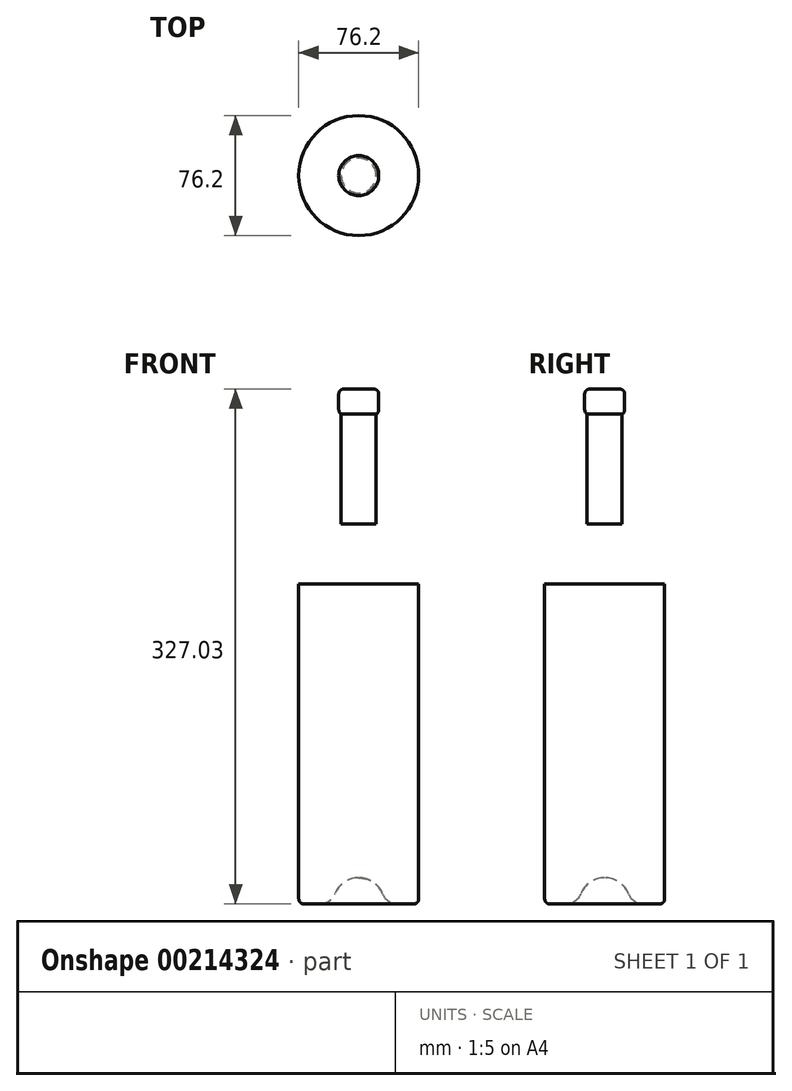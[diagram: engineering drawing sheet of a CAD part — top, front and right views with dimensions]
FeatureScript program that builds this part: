
annotation { "Feature Type Name" : "Feature", "Feature Type Description" : "" }
export const myFeature = defineFeature(function(context is Context, id is Id, definition is map)
    precondition{}
    {
        {
            var Q0;
            Q0=qCreatedBy(makeId("Front.planeOp"),FACE);
            var sketch = newSketch(context, id + "F0", { "sketchPlane" : qUnion([Q0])});
            skLineSegment(sketch, "E0.bottom", {"start": v(38.1, 101.6) * mm, "end": v(-38.1, 101.6) * mm});
            skLineSegment(sketch, "E0.top", {"start": v(38.1, -101.6) * mm, "end": v(24.45, -101.6) * mm});
            skLineSegment(sketch, "E0.left", {"start": v(38.1, 101.6) * mm, "end": v(38.1, -101.6) * mm});
            skLineSegment(sketch, "E0.right", {"start": v(-38.1, 101.6) * mm, "end": v(-38.1, -101.6) * mm});
            skPoint(sketch, "E0.middle", {"position": v(0, 0) * mm});
            skLineSegment(sketch, "E1.bottom", {"start": v(11.11, 225.42) * mm, "end": v(-11.11, 225.42) * mm});
            skLineSegment(sketch, "E1.top", {"start": v(11.11, 139.7) * mm, "end": v(-11.11, 139.7) * mm});
            skLineSegment(sketch, "E1.left", {"start": v(11.11, 225.42) * mm, "end": v(11.11, 139.7) * mm});
            skLineSegment(sketch, "E1.right", {"start": v(-11.11, 225.42) * mm, "end": v(-11.11, 139.7) * mm});
            skPoint(sketch, "E1.middle", {"position": v(0, 182.56) * mm});
            skLineSegment(sketch, "E2", {"start": v(0, 0) * mm, "end": v(0, 182.56) * mm, "construction": true});
            skLineSegment(sketch, "E3.bottom", {"start": v(12.7, 225.42) * mm, "end": v(-12.7, 225.42) * mm});
            skLineSegment(sketch, "E3.top", {"start": v(12.7, 209.55) * mm, "end": v(-12.7, 209.55) * mm});
            skLineSegment(sketch, "E3.left", {"start": v(12.7, 225.42) * mm, "end": v(12.7, 209.55) * mm});
            skLineSegment(sketch, "E3.right", {"start": v(-12.7, 225.42) * mm, "end": v(-12.7, 209.55) * mm});
            skPoint(sketch, "E3.middle", {"position": v(0, 217.49) * mm});
            skPoint(sketch, "E3.cornerSnap0", {"position": v(0, 225.42) * mm});
            skLineSegment(sketch, "E4", {"start": v(0, -85.04) * mm, "end": v(0, -101.6) * mm, "construction": true});
            skLineSegment(sketch, "E5.trimOffspring", {"start": v(-24.45, -101.6) * mm, "end": v(-38.1, -101.6) * mm});
            skArc(sketch, "E6", {"start": v(-24.45, -101.6) * mm, "mid": v(-18.89, -99.9) * mm, "end": v(-15.24, -95.36) * mm});
            skArc(sketch, "E7", {"start": v(-15.24, -95.36) * mm, "mid": v(-9.2, -87.87) * mm, "end": v(0, -85.04) * mm});
            skLineSegment(sketch, "E8", {"start": v(0, -85.04) * mm, "end": v(-15.84, -85.04) * mm, "construction": true});
            skArc(sketch, "E9.MirrorCS", {"start": v(15.24, -95.36) * mm, "mid": v(9.2, -87.87) * mm, "end": v(0, -85.04) * mm});
            skArc(sketch, "E10.MirrorCS", {"start": v(24.45, -101.6) * mm, "mid": v(18.89, -99.9) * mm, "end": v(15.24, -95.36) * mm});
            skArc(sketch, "E11", {"start": v(-38.1, 101.6) * mm, "mid": v(-34.06, 114.39) * mm, "end": v(-23.4, 122.53) * mm});
            skArc(sketch, "E12", {"start": v(-23.4, 122.53) * mm, "mid": v(-14.59, 129.2) * mm, "end": v(-11.11, 139.7) * mm});
            skArc(sketch, "E13.MirrorCS", {"start": v(23.4, 122.53) * mm, "mid": v(14.59, 129.2) * mm, "end": v(11.11, 139.7) * mm});
            skArc(sketch, "E14.MirrorCS", {"start": v(38.1, 101.6) * mm, "mid": v(34.06, 114.39) * mm, "end": v(23.4, 122.53) * mm});
            skLineSegment(sketch, "E15", {"start": v(0, -85.04) * mm, "end": v(0, 225.42) * mm});
            skSolve(sketch);
        }
        {
            var Q0;
            {var subQ5=sQuery(id+"F0.wireOp",EDGE,"E3.right");Q0=makeQuery(id+"F0.imprint","IMPRINT",FACE,{"disambiguationData":[TD([[makeQuery(id+"F0.imprint","IMPRINT",EDGE,{"derivedFrom":subQ5}),1.0]])]});}
            var Q1;
            {var subQ0=sQuery(id+"F0.wireOp",EDGE,"E3.bottom");var subQ1=sQuery(id+"F0.wireOp",EDGE,"E1.right");var subQ2=makeQuery(id+"F0.imprint","INTERSECT",VERTEX,{"derivedFrom":[subQ1,subQ0]});Q1=makeQuery(id+"F0.imprint","IMPRINT",FACE,{"disambiguationData":[TD([[makeQuery(id+"F0.imprint","IMPRINT",EDGE,{"disambiguationData":[TD([[subQ2,-1.0]])],"derivedFrom":subQ1}),1.0]])]});}
            var Q2;
            {var subQ0=sQuery(id+"F0.wireOp",EDGE,"E1.right");var subQ5=sQuery(id+"F0.wireOp",EDGE,"E3.top");var subQ6=makeQuery(id+"F0.imprint","INTERSECT",VERTEX,{"derivedFrom":[subQ0,subQ5]});Q2=makeQuery(id+"F0.imprint","IMPRINT",FACE,{"disambiguationData":[TD([[makeQuery(id+"F0.imprint","IMPRINT",EDGE,{"disambiguationData":[TD([[subQ6,1.0]])],"derivedFrom":subQ5}),1.0]])]});}
            var Q3;
            {var subQ1=sQuery(id+"F0.wireOp",EDGE,"E11");Q3=makeQuery(id+"F0.imprint","IMPRINT",FACE,{"disambiguationData":[TD([[makeQuery(id+"F0.imprint","IMPRINT",EDGE,{"derivedFrom":subQ1}),-1.0]])]});}
            var Q4;
            {var subQ1=sQuery(id+"F0.wireOp",EDGE,"E0.right");Q4=makeQuery(id+"F0.imprint","IMPRINT",FACE,{"disambiguationData":[TD([[makeQuery(id+"F0.imprint","IMPRINT",EDGE,{"derivedFrom":subQ1}),1.0]])]});}
            var Q5;
            Q5=sQuery(id+"F0.wireOp",EDGE,"E15");
            revolve(context, id + "F1", {"entities" : qUnion([Q0, Q1, Q2, Q3, Q4]), "axis" : qUnion([Q5]), "revolveType" : RevolveType.FULL});
        }
        {
            var Q0;
            Q0=makeQuery(id+"F1.opRevolve","SWEPT_EDGE",EDGE,{"disambiguationData":[OSD([sQuery(id+"F0.wireOp",EDGE,"E0.right"),sQuery(id+"F0.wireOp",EDGE,"E5.trimOffspring")])]});
            var Q1;
            Q1=makeQuery(id+"F1.opRevolve","SWEPT_EDGE",EDGE,{"disambiguationData":[OSD([sQuery(id+"F0.wireOp",EDGE,"E3.bottom"),sQuery(id+"F0.wireOp",EDGE,"E3.right")])]});
            var Q2;
            Q2=makeQuery(id+"F1.opRevolve","SWEPT_EDGE",EDGE,{"disambiguationData":[OSD([sQuery(id+"F0.wireOp",EDGE,"E3.top"),sQuery(id+"F0.wireOp",EDGE,"E3.right")])]});
            fillet(context, id + "F2", {"entities" : qUnion([Q0, Q1, Q2]), "radius" : 3.17 * mm, "tangentPropagation" : true, "allowEdgeOverflow" : false});
        }
    });
